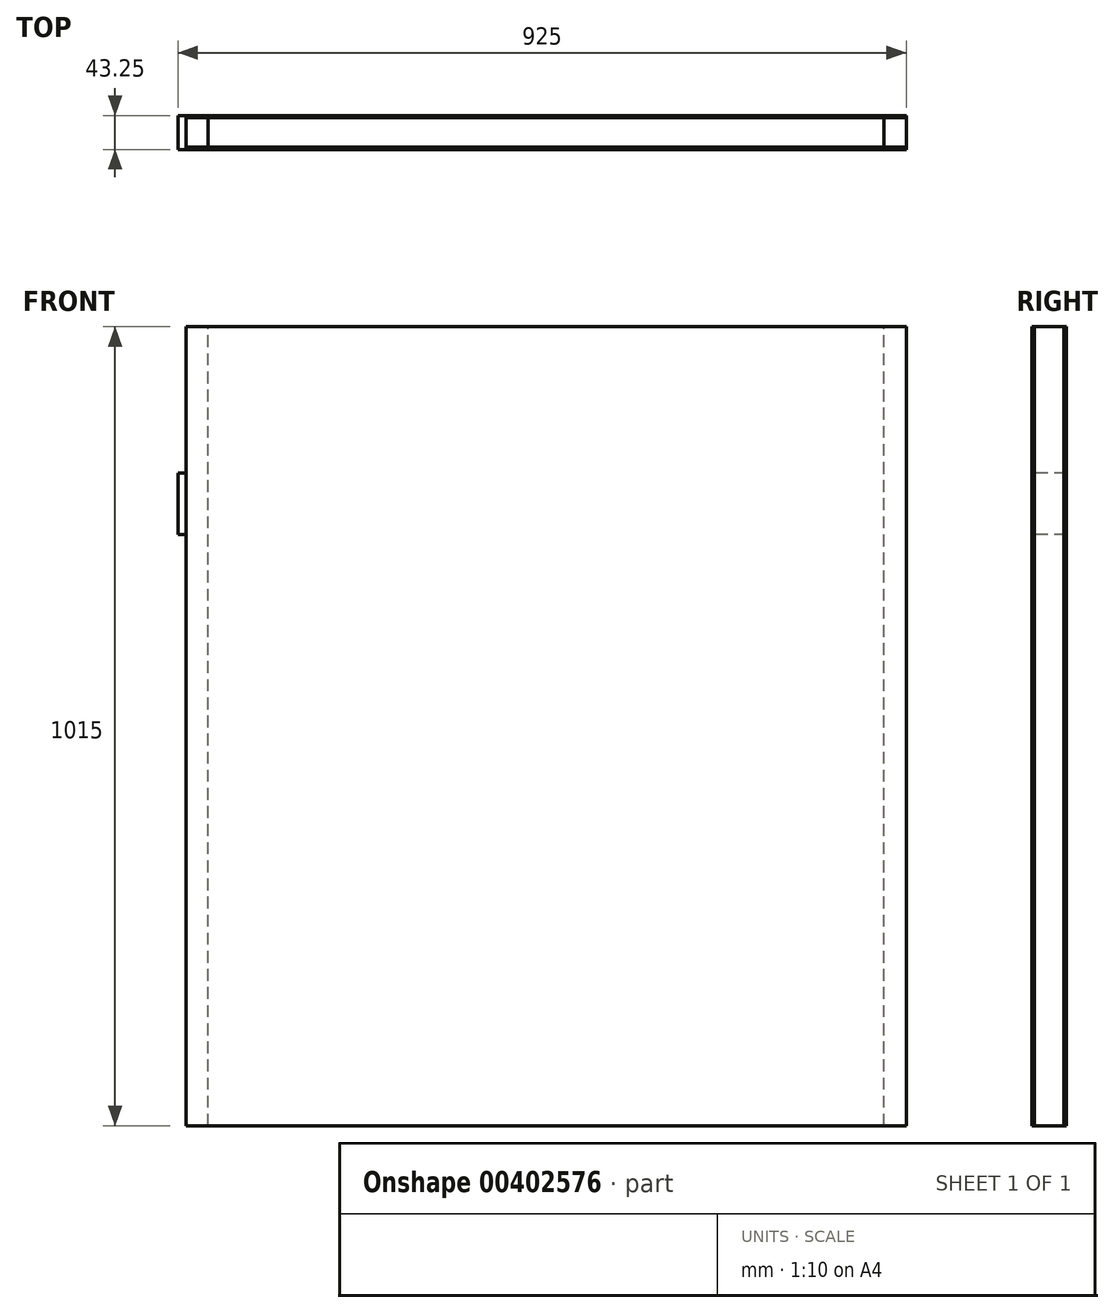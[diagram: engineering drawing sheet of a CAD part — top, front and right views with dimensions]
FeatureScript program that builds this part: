
annotation { "Feature Type Name" : "Feature", "Feature Type Description" : "" }
export const myFeature = defineFeature(function(context is Context, id is Id, definition is map)
    precondition{}
    {
        {
            var Q0;
            Q0=qCreatedBy(makeId("Front.planeOp"),FACE);
            var sketch = newSketch(context, id + "F0", { "sketchPlane" : qUnion([Q0])});
            skLineSegment(sketch, "E0.bottom", {"start": v(-457.5, 507.5) * mm, "end": v(457.5, 507.5) * mm});
            skLineSegment(sketch, "E0.top", {"start": v(-457.5, -507.5) * mm, "end": v(457.5, -507.5) * mm});
            skLineSegment(sketch, "E0.left", {"start": v(-457.5, 507.5) * mm, "end": v(-457.5, -507.5) * mm});
            skLineSegment(sketch, "E0.right", {"start": v(457.5, 507.5) * mm, "end": v(457.5, -507.5) * mm});
            skPoint(sketch, "E0.middle", {"position": v(0, 0) * mm});
            skSolve(sketch);
        }
        {
            var Q0;
            Q0=makeQuery(id+"F0.imprint","IMPRINT",FACE,{"disambiguationData":[TD([[makeQuery(id+"F0.imprint","IMPRINT",EDGE,{"derivedFrom":sQuery(id+"F0.wireOp",EDGE,"E0.bottom")}),-1.0]])]});
            extrude(context, id + "F1", {"entities" : qUnion([Q0]), "depth" : 43.25 * mm});
        }
        {
            var Q0;
            Q0=makeQuery(id+"F1.opExtrude","CAP_FACE",FACE,{"disambiguationData":[OSD([sQuery(id+"F0.wireOp",EDGE,"E0.bottom"),sQuery(id+"F0.wireOp",EDGE,"E0.top"),sQuery(id+"F0.wireOp",EDGE,"E0.left"),sQuery(id+"F0.wireOp",EDGE,"E0.right")])],"isStart":false});
            extrude(context, id + "F2", {"entities" : qUnion([Q0]), "oppositeDirection" : true, "depth" : 2.81 * mm});
        }
        {
            var Q0;
            Q0=makeQuery(id+"F1.opExtrude","CAP_FACE",FACE,{"disambiguationData":[OSD([sQuery(id+"F0.wireOp",EDGE,"E0.bottom"),sQuery(id+"F0.wireOp",EDGE,"E0.top"),sQuery(id+"F0.wireOp",EDGE,"E0.left"),sQuery(id+"F0.wireOp",EDGE,"E0.right")])],"isStart":true});
            extrude(context, id + "F3", {"entities" : qUnion([Q0]), "oppositeDirection" : true, "depth" : 2.81 * mm});
        }
        {
            var Q0;
            Q0=makeQuery(id+"F1.opExtrude","CAP_FACE",FACE,{"disambiguationData":[OSD([sQuery(id+"F0.wireOp",EDGE,"E0.bottom"),sQuery(id+"F0.wireOp",EDGE,"E0.top"),sQuery(id+"F0.wireOp",EDGE,"E0.left"),sQuery(id+"F0.wireOp",EDGE,"E0.right")])],"isStart":false});
            var sketch = newSketch(context, id + "F4", { "sketchPlane" : qUnion([Q0])});
            skLineSegment(sketch, "E1", {"start": v(-457.5, 507.5) * mm, "end": v(-457.5, 321.5) * mm});
            skLineSegment(sketch, "E2", {"start": v(-457.5, 321.5) * mm, "end": v(-467.5, 321.5) * mm});
            skLineSegment(sketch, "E3", {"start": v(-467.5, 321.5) * mm, "end": v(-467.5, 243.5) * mm});
            skLineSegment(sketch, "E4", {"start": v(-467.5, 243.5) * mm, "end": v(-457.5, 243.5) * mm});
            skSolve(sketch);
        }
        {
            var Q0;
            {var subQ0=sQuery(id+"F4.wireOp",EDGE,"E2");Q0=makeQuery(id+"F4.imprint","IMPRINT",FACE,{"disambiguationData":[TD([[makeQuery(id+"F4.imprint","IMPRINT",EDGE,{"derivedFrom":subQ0}),1.0]])]});}
            extrude(context, id + "F5", {"entities" : qUnion([Q0]), "oppositeDirection" : true, "depth" : 43 * mm});
        }
        {
            var Q0;
            Q0=makeQuery(id+"F1.opExtrude","SWEPT_FACE",FACE,{"disambiguationData":[OSD([sQuery(id+"F0.wireOp",EDGE,"E0.bottom")])]});
            var sketch = newSketch(context, id + "F6", { "sketchPlane" : qUnion([Q0])});
            skLineSegment(sketch, "E5", {"start": v(-457.5, -2.81) * mm, "end": v(-457.5, -2.81) * mm});
            skLineSegment(sketch, "E6", {"start": v(-429.5, -2.81) * mm, "end": v(-429.5, -2.81) * mm});
            skLineSegment(sketch, "E7", {"start": v(-429.5, -40.44) * mm, "end": v(-429.5, -40.44) * mm});
            skLineSegment(sketch, "E8", {"start": v(-457.5, -2.81) * mm, "end": v(-457.5, -40.44) * mm});
            skLineSegment(sketch, "E9", {"start": v(-457.5, -2.81) * mm, "end": v(-429.5, -2.81) * mm});
            skLineSegment(sketch, "E10", {"start": v(-457.5, -40.44) * mm, "end": v(-457.5, -40.44) * mm});
            skLineSegment(sketch, "E11", {"start": v(-429.5, -40.44) * mm, "end": v(-457.5, -40.44) * mm});
            skLineSegment(sketch, "E12", {"start": v(-429.5, -2.81) * mm, "end": v(-429.5, -40.44) * mm});
            skLineSegment(sketch, "E13", {"start": v(457.5, -2.81) * mm, "end": v(429.5, -2.81) * mm});
            skLineSegment(sketch, "E14", {"start": v(429.5, -2.81) * mm, "end": v(429.5, -40.44) * mm});
            skLineSegment(sketch, "E15", {"start": v(429.5, -40.44) * mm, "end": v(429.5, -40.44) * mm});
            skLineSegment(sketch, "E16", {"start": v(429.5, -40.44) * mm, "end": v(457.5, -40.44) * mm});
            skLineSegment(sketch, "E17", {"start": v(457.5, -40.44) * mm, "end": v(457.5, -2.81) * mm});
            skSolve(sketch);
        }
        {
            var Q0;
            Q0=makeQuery(id+"F6.imprint","IMPRINT",FACE,{"disambiguationData":[TD([[makeQuery(id+"F6.imprint","IMPRINT",EDGE,{"derivedFrom":sQuery(id+"F6.wireOp",EDGE,"E13")}),1.0]])]});
            var Q1;
            Q1=makeQuery(id+"F6.imprint","IMPRINT",FACE,{"disambiguationData":[TD([[makeQuery(id+"F6.imprint","IMPRINT",EDGE,{"derivedFrom":sQuery(id+"F6.wireOp",EDGE,"E8")}),-1.0]])]});
            extrude(context, id + "F7", {"entities" : qUnion([Q0, Q1]), "endBound" : BoundingType.UP_TO_NEXT, "oppositeDirection" : true, "depth" : 25 * mm});
        }
    });
